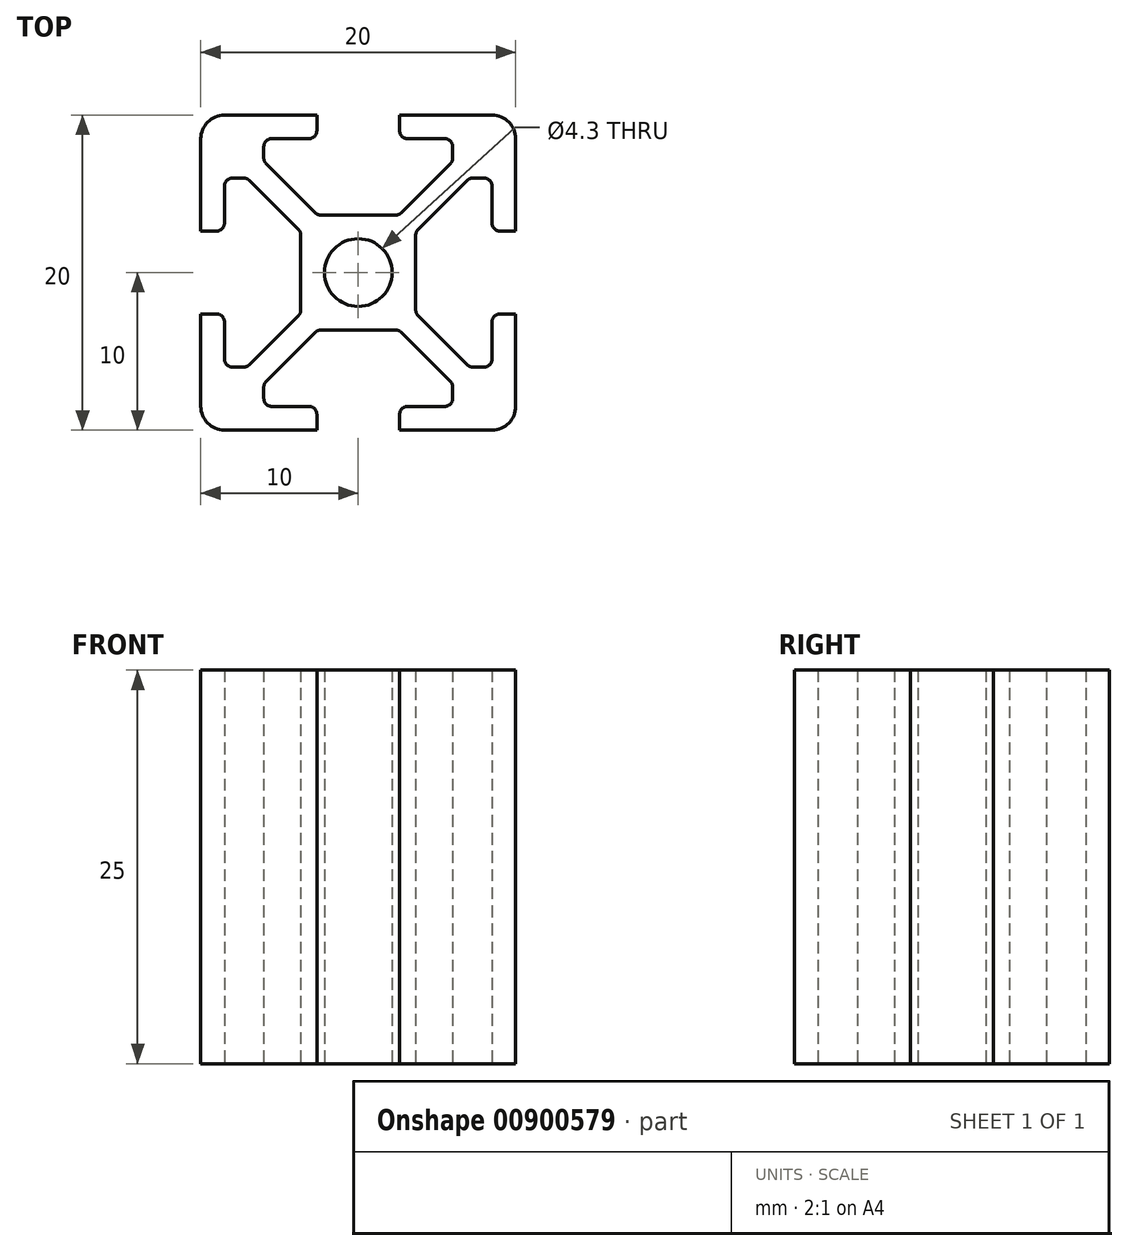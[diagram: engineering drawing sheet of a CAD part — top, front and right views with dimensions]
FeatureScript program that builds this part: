
annotation { "Feature Type Name" : "Feature", "Feature Type Description" : "" }
export const myFeature = defineFeature(function(context is Context, id is Id, definition is map)
    precondition{}
    {
        {
            var Q0;
            Q0=qCreatedBy(makeId("Top.planeOp"),FACE);
            var sketch = newSketch(context, id + "F0", { "sketchPlane" : qUnion([Q0])});
            skPoint(sketch, "E0.middle", {"position": v(0, 0) * mm});
            skCircle(sketch, "E1", {"center": v(0, 0) * mm, "radius": 2.15 * mm});
            skLineSegment(sketch, "E2.bottom", {"start": v(10, 10) * mm, "end": v(-10, 10) * mm});
            skLineSegment(sketch, "E2.top", {"start": v(10, -10) * mm, "end": v(-10, -10) * mm});
            skLineSegment(sketch, "E2.left", {"start": v(10, 10) * mm, "end": v(10, -10) * mm});
            skLineSegment(sketch, "E2.right", {"start": v(-10, 10) * mm, "end": v(-10, -10) * mm});
            skSolve(sketch);
        }
        {
            var Q0;
            Q0=makeQuery(id+"F0.imprint","IMPRINT",FACE,{"disambiguationData":[TD([[makeQuery(id+"F0.imprint","IMPRINT",EDGE,{"derivedFrom":sQuery(id+"F0.wireOp",EDGE,"E1")}),-1.0]])]});
            var sketch = newSketch(context, id + "F1", { "sketchPlane" : qUnion([Q0])});
            skLineSegment(sketch, "E3", {"start": v(-2.63, 10) * mm, "end": v(2.63, 10) * mm});
            skLineSegment(sketch, "E4", {"start": v(2.63, 10) * mm, "end": v(2.63, 8.5) * mm});
            skLineSegment(sketch, "E5", {"start": v(2.63, 8.5) * mm, "end": v(6, 8.5) * mm});
            skLineSegment(sketch, "E6", {"start": v(6, 8.5) * mm, "end": v(6, 7.06) * mm});
            skLineSegment(sketch, "E7", {"start": v(6, 7.06) * mm, "end": v(2.59, 3.65) * mm});
            skLineSegment(sketch, "E8", {"start": v(2.59, 3.65) * mm, "end": v(-2.59, 3.65) * mm});
            skLineSegment(sketch, "E9", {"start": v(-2.59, 3.65) * mm, "end": v(-6, 7.06) * mm});
            skLineSegment(sketch, "E10", {"start": v(-6, 7.06) * mm, "end": v(-6, 8.5) * mm});
            skLineSegment(sketch, "E11", {"start": v(-6, 8.5) * mm, "end": v(-2.63, 8.5) * mm});
            skLineSegment(sketch, "E12", {"start": v(-2.63, 8.5) * mm, "end": v(-2.63, 10) * mm});
            skPoint(sketch, "E13", {"position": v(0, 10) * mm});
            skPoint(sketch, "E14", {"position": v(0, 3.65) * mm});
            skPoint(sketch, "E15.center", {"position": v(0.01, -0.04) * mm});
            skLineSegment(sketch, "E16.0.0", {"start": v(-10, -10) * mm, "end": v(10, -10) * mm});
            skLineSegment(sketch, "E16.0.1", {"start": v(10, -10) * mm, "end": v(10, 10) * mm});
            skLineSegment(sketch, "E16.0.2", {"start": v(10, 10) * mm, "end": v(-10, 10) * mm});
            skLineSegment(sketch, "E16.0.3", {"start": v(-10, 10) * mm, "end": v(-10, -10) * mm});
            skLineSegment(sketch, "E17", {"start": v(0, 0) * mm, "end": v(10, 10) * mm, "construction": true});
            skLineSegment(sketch, "E18.1.0", {"start": v(-8.5, -2.63) * mm, "end": v(-10, -2.63) * mm});
            skLineSegment(sketch, "E18.1.1", {"start": v(-8.5, -6) * mm, "end": v(-8.5, -2.63) * mm});
            skLineSegment(sketch, "E18.1.2", {"start": v(-7.06, -6) * mm, "end": v(-8.5, -6) * mm});
            skLineSegment(sketch, "E18.1.3", {"start": v(-3.65, -2.59) * mm, "end": v(-7.06, -6) * mm});
            skLineSegment(sketch, "E18.1.4", {"start": v(-3.65, 2.59) * mm, "end": v(-3.65, -2.59) * mm});
            skLineSegment(sketch, "E18.1.5", {"start": v(-7.06, 6) * mm, "end": v(-3.65, 2.59) * mm});
            skLineSegment(sketch, "E18.1.6", {"start": v(-8.5, 6) * mm, "end": v(-7.06, 6) * mm});
            skLineSegment(sketch, "E18.1.7", {"start": v(-8.5, 2.63) * mm, "end": v(-8.5, 6) * mm});
            skLineSegment(sketch, "E18.1.8", {"start": v(-10, 2.63) * mm, "end": v(-8.5, 2.63) * mm});
            skLineSegment(sketch, "E18.2.0", {"start": v(2.63, -8.5) * mm, "end": v(2.63, -10) * mm});
            skLineSegment(sketch, "E18.2.1", {"start": v(6, -8.5) * mm, "end": v(2.63, -8.5) * mm});
            skLineSegment(sketch, "E18.2.2", {"start": v(6, -7.06) * mm, "end": v(6, -8.5) * mm});
            skLineSegment(sketch, "E18.2.3", {"start": v(2.59, -3.65) * mm, "end": v(6, -7.06) * mm});
            skLineSegment(sketch, "E18.2.4", {"start": v(-2.59, -3.65) * mm, "end": v(2.59, -3.65) * mm});
            skLineSegment(sketch, "E18.2.5", {"start": v(-6, -7.06) * mm, "end": v(-2.59, -3.65) * mm});
            skLineSegment(sketch, "E18.2.6", {"start": v(-6, -8.5) * mm, "end": v(-6, -7.06) * mm});
            skLineSegment(sketch, "E18.2.7", {"start": v(-2.63, -8.5) * mm, "end": v(-6, -8.5) * mm});
            skLineSegment(sketch, "E18.2.8", {"start": v(-2.63, -10) * mm, "end": v(-2.63, -8.5) * mm});
            skLineSegment(sketch, "E18.3.0", {"start": v(8.5, 2.63) * mm, "end": v(10, 2.63) * mm});
            skLineSegment(sketch, "E18.3.1", {"start": v(8.5, 6) * mm, "end": v(8.5, 2.63) * mm});
            skLineSegment(sketch, "E18.3.2", {"start": v(7.06, 6) * mm, "end": v(8.5, 6) * mm});
            skLineSegment(sketch, "E18.3.3", {"start": v(3.65, 2.59) * mm, "end": v(7.06, 6) * mm});
            skLineSegment(sketch, "E18.3.4", {"start": v(3.65, -2.59) * mm, "end": v(3.65, 2.59) * mm});
            skLineSegment(sketch, "E18.3.5", {"start": v(7.06, -6) * mm, "end": v(3.65, -2.59) * mm});
            skLineSegment(sketch, "E18.3.6", {"start": v(8.5, -6) * mm, "end": v(7.06, -6) * mm});
            skLineSegment(sketch, "E18.3.7", {"start": v(8.5, -2.63) * mm, "end": v(8.5, -6) * mm});
            skLineSegment(sketch, "E18.3.8", {"start": v(10, -2.63) * mm, "end": v(8.5, -2.63) * mm});
            skPoint(sketch, "E18.center", {"position": v(0, 0) * mm});
            skSolve(sketch);
        }
        {
            var Q0;
            Q0=makeQuery(id+"F0.imprint","IMPRINT",FACE,{"disambiguationData":[TD([[makeQuery(id+"F0.imprint","IMPRINT",EDGE,{"derivedFrom":sQuery(id+"F0.wireOp",EDGE,"E1")}),-1.0]])]});
            extrude(context, id + "F2", {"entities" : qUnion([Q0]), "depth" : 25 * mm, "offsetDistance" : 25 * mm});
        }
        {
            var Q0;
            {var subQ0=sQuery(id+"F1.wireOp",EDGE,"E18.1.0");Q0=makeQuery(id+"F1.imprint","IMPRINT",FACE,{"disambiguationData":[TD([[makeQuery(id+"F1.imprint","IMPRINT",EDGE,{"derivedFrom":subQ0}),-1.0]])]});}
            var Q1;
            {var subQ0=sQuery(id+"F1.wireOp",EDGE,"E18.2.0");Q1=makeQuery(id+"F1.imprint","IMPRINT",FACE,{"disambiguationData":[TD([[makeQuery(id+"F1.imprint","IMPRINT",EDGE,{"derivedFrom":subQ0}),-1.0]])]});}
            var Q2;
            {var subQ0=sQuery(id+"F1.wireOp",EDGE,"E18.3.0");Q2=makeQuery(id+"F1.imprint","IMPRINT",FACE,{"disambiguationData":[TD([[makeQuery(id+"F1.imprint","IMPRINT",EDGE,{"derivedFrom":subQ0}),-1.0]])]});}
            var Q3;
            {var subQ0=sQuery(id+"F1.wireOp",EDGE,"E4");Q3=makeQuery(id+"F1.imprint","IMPRINT",FACE,{"disambiguationData":[TD([[makeQuery(id+"F1.imprint","IMPRINT",EDGE,{"derivedFrom":subQ0}),-1.0]])]});}
            extrude(context, id + "F3", {"entities" : qUnion([Q0, Q1, Q2, Q3]), "operationType" : NewBodyOperationType.REMOVE, "endBound" : BoundingType.THROUGH_ALL, "depth" : 25 * mm, "offsetDistance" : 25 * mm});
        }
        {
            var Q0;
            Q0=makeQuery(id+"F2.opExtrude","SWEPT_EDGE",EDGE,{"disambiguationData":[OSD([sQuery(id+"F0.wireOp",EDGE,"E2.top"),sQuery(id+"F0.wireOp",EDGE,"E2.left")])]});
            var Q1;
            Q1=makeQuery(id+"F2.opExtrude","SWEPT_EDGE",EDGE,{"disambiguationData":[OSD([sQuery(id+"F0.wireOp",EDGE,"E2.top"),sQuery(id+"F0.wireOp",EDGE,"E2.right")])]});
            var Q2;
            Q2=makeQuery(id+"F2.opExtrude","SWEPT_EDGE",EDGE,{"disambiguationData":[OSD([sQuery(id+"F0.wireOp",EDGE,"E2.bottom"),sQuery(id+"F0.wireOp",EDGE,"E2.left")])]});
            var Q3;
            Q3=makeQuery(id+"F2.opExtrude","SWEPT_EDGE",EDGE,{"disambiguationData":[OSD([sQuery(id+"F0.wireOp",EDGE,"E2.bottom"),sQuery(id+"F0.wireOp",EDGE,"E2.right")])]});
            fillet(context, id + "F4", {"entities" : qUnion([Q0, Q1, Q2, Q3]), "radius" : 1.5 * mm, "tangentPropagation" : true, "allowEdgeOverflow" : false});
        }
        {
            var Q0;
            Q0=makeQuery(id+"F3.boolean.opBoolean","COPY",EDGE,{"derivedFrom":makeQuery(id+"F3.opExtrude","SWEPT_EDGE",EDGE,{"disambiguationData":[OSD([sQuery(id+"F1.wireOp",EDGE,"E16.0.0"),sQuery(id+"F1.wireOp",EDGE,"E18.2.8")])]})});
            var Q1;
            Q1=makeQuery(id+"F3.boolean.opBoolean","COPY",EDGE,{"derivedFrom":makeQuery(id+"F3.opExtrude","SWEPT_EDGE",EDGE,{"disambiguationData":[OSD([sQuery(id+"F1.wireOp",EDGE,"E16.0.3"),sQuery(id+"F1.wireOp",EDGE,"E18.1.8")])]})});
            var Q2;
            Q2=makeQuery(id+"F3.boolean.opBoolean","COPY",EDGE,{"derivedFrom":makeQuery(id+"F3.opExtrude","SWEPT_EDGE",EDGE,{"disambiguationData":[OSD([sQuery(id+"F1.wireOp",EDGE,"E12"),sQuery(id+"F1.wireOp",EDGE,"E16.0.2")])]})});
            var Q3;
            Q3=makeQuery(id+"F3.boolean.opBoolean","COPY",EDGE,{"derivedFrom":makeQuery(id+"F3.opExtrude","SWEPT_EDGE",EDGE,{"disambiguationData":[OSD([sQuery(id+"F1.wireOp",EDGE,"E16.0.0"),sQuery(id+"F1.wireOp",EDGE,"E18.2.0")])]})});
            var Q4;
            Q4=makeQuery(id+"F3.boolean.opBoolean","COPY",EDGE,{"derivedFrom":makeQuery(id+"F3.opExtrude","SWEPT_EDGE",EDGE,{"disambiguationData":[OSD([sQuery(id+"F1.wireOp",EDGE,"E16.0.1"),sQuery(id+"F1.wireOp",EDGE,"E18.3.0")])]})});
            var Q5;
            Q5=makeQuery(id+"F3.boolean.opBoolean","COPY",EDGE,{"derivedFrom":makeQuery(id+"F3.opExtrude","SWEPT_EDGE",EDGE,{"disambiguationData":[OSD([sQuery(id+"F1.wireOp",EDGE,"E16.0.1"),sQuery(id+"F1.wireOp",EDGE,"E18.3.8")])]})});
            var Q6;
            Q6=makeQuery(id+"F3.boolean.opBoolean","COPY",EDGE,{"derivedFrom":makeQuery(id+"F3.opExtrude","SWEPT_EDGE",EDGE,{"disambiguationData":[OSD([sQuery(id+"F1.wireOp",EDGE,"E16.0.3"),sQuery(id+"F1.wireOp",EDGE,"E18.1.0")])]})});
            var Q7;
            Q7=makeQuery(id+"F3.boolean.opBoolean","COPY",EDGE,{"derivedFrom":makeQuery(id+"F3.opExtrude","SWEPT_EDGE",EDGE,{"disambiguationData":[OSD([sQuery(id+"F1.wireOp",EDGE,"E4"),sQuery(id+"F1.wireOp",EDGE,"E16.0.2")])]})});
            var Q8;
            Q8=makeQuery(id+"F3.boolean.opBoolean","COPY",EDGE,{"derivedFrom":makeQuery(id+"F3.opExtrude","SWEPT_EDGE",EDGE,{"disambiguationData":[OSD([sQuery(id+"F1.wireOp",EDGE,"E18.2.6"),sQuery(id+"F1.wireOp",EDGE,"E18.2.7")])]})});
            var Q9;
            Q9=makeQuery(id+"F3.boolean.opBoolean","COPY",EDGE,{"derivedFrom":makeQuery(id+"F3.opExtrude","SWEPT_EDGE",EDGE,{"disambiguationData":[OSD([sQuery(id+"F1.wireOp",EDGE,"E18.2.7"),sQuery(id+"F1.wireOp",EDGE,"E18.2.8")])]})});
            var Q10;
            Q10=makeQuery(id+"F3.boolean.opBoolean","COPY",EDGE,{"derivedFrom":makeQuery(id+"F3.opExtrude","SWEPT_EDGE",EDGE,{"disambiguationData":[OSD([sQuery(id+"F1.wireOp",EDGE,"E18.2.0"),sQuery(id+"F1.wireOp",EDGE,"E18.2.1")])]})});
            var Q11;
            Q11=makeQuery(id+"F3.boolean.opBoolean","COPY",EDGE,{"derivedFrom":makeQuery(id+"F3.opExtrude","SWEPT_EDGE",EDGE,{"disambiguationData":[OSD([sQuery(id+"F1.wireOp",EDGE,"E18.1.7"),sQuery(id+"F1.wireOp",EDGE,"E18.1.8")])]})});
            var Q12;
            Q12=makeQuery(id+"F3.boolean.opBoolean","COPY",EDGE,{"derivedFrom":makeQuery(id+"F3.opExtrude","SWEPT_EDGE",EDGE,{"disambiguationData":[OSD([sQuery(id+"F1.wireOp",EDGE,"E18.1.0"),sQuery(id+"F1.wireOp",EDGE,"E18.1.1")])]})});
            var Q13;
            Q13=makeQuery(id+"F3.boolean.opBoolean","COPY",EDGE,{"derivedFrom":makeQuery(id+"F3.opExtrude","SWEPT_EDGE",EDGE,{"disambiguationData":[OSD([sQuery(id+"F1.wireOp",EDGE,"E18.3.7"),sQuery(id+"F1.wireOp",EDGE,"E18.3.8")])]})});
            var Q14;
            Q14=makeQuery(id+"F3.boolean.opBoolean","COPY",EDGE,{"derivedFrom":makeQuery(id+"F3.opExtrude","SWEPT_EDGE",EDGE,{"disambiguationData":[OSD([sQuery(id+"F1.wireOp",EDGE,"E18.3.0"),sQuery(id+"F1.wireOp",EDGE,"E18.3.1")])]})});
            var Q15;
            Q15=makeQuery(id+"F3.boolean.opBoolean","COPY",EDGE,{"derivedFrom":makeQuery(id+"F3.opExtrude","SWEPT_EDGE",EDGE,{"disambiguationData":[OSD([sQuery(id+"F1.wireOp",EDGE,"E4"),sQuery(id+"F1.wireOp",EDGE,"E5")])]})});
            var Q16;
            Q16=makeQuery(id+"F3.boolean.opBoolean","COPY",EDGE,{"derivedFrom":makeQuery(id+"F3.opExtrude","SWEPT_EDGE",EDGE,{"disambiguationData":[OSD([sQuery(id+"F1.wireOp",EDGE,"E5"),sQuery(id+"F1.wireOp",EDGE,"E6")])]})});
            var Q17;
            Q17=makeQuery(id+"F3.boolean.opBoolean","COPY",EDGE,{"derivedFrom":makeQuery(id+"F3.opExtrude","SWEPT_EDGE",EDGE,{"disambiguationData":[OSD([sQuery(id+"F1.wireOp",EDGE,"E18.3.1"),sQuery(id+"F1.wireOp",EDGE,"E18.3.2")])]})});
            var Q18;
            Q18=makeQuery(id+"F3.boolean.opBoolean","COPY",EDGE,{"derivedFrom":makeQuery(id+"F3.opExtrude","SWEPT_EDGE",EDGE,{"disambiguationData":[OSD([sQuery(id+"F1.wireOp",EDGE,"E18.3.2"),sQuery(id+"F1.wireOp",EDGE,"E18.3.3")])]})});
            var Q19;
            Q19=makeQuery(id+"F3.boolean.opBoolean","COPY",EDGE,{"derivedFrom":makeQuery(id+"F3.opExtrude","SWEPT_EDGE",EDGE,{"disambiguationData":[OSD([sQuery(id+"F1.wireOp",EDGE,"E6"),sQuery(id+"F1.wireOp",EDGE,"E7")])]})});
            var Q20;
            Q20=makeQuery(id+"F3.boolean.opBoolean","COPY",EDGE,{"derivedFrom":makeQuery(id+"F3.opExtrude","SWEPT_EDGE",EDGE,{"disambiguationData":[OSD([sQuery(id+"F1.wireOp",EDGE,"E18.2.4"),sQuery(id+"F1.wireOp",EDGE,"E18.2.5")])]})});
            var Q21;
            Q21=makeQuery(id+"F3.boolean.opBoolean","COPY",EDGE,{"derivedFrom":makeQuery(id+"F3.opExtrude","SWEPT_EDGE",EDGE,{"disambiguationData":[OSD([sQuery(id+"F1.wireOp",EDGE,"E18.2.3"),sQuery(id+"F1.wireOp",EDGE,"E18.2.4")])]})});
            var Q22;
            Q22=makeQuery(id+"F3.boolean.opBoolean","COPY",EDGE,{"derivedFrom":makeQuery(id+"F3.opExtrude","SWEPT_EDGE",EDGE,{"disambiguationData":[OSD([sQuery(id+"F1.wireOp",EDGE,"E18.3.3"),sQuery(id+"F1.wireOp",EDGE,"E18.3.4")])]})});
            var Q23;
            Q23=makeQuery(id+"F3.boolean.opBoolean","COPY",EDGE,{"derivedFrom":makeQuery(id+"F3.opExtrude","SWEPT_EDGE",EDGE,{"disambiguationData":[OSD([sQuery(id+"F1.wireOp",EDGE,"E18.3.4"),sQuery(id+"F1.wireOp",EDGE,"E18.3.5")])]})});
            var Q24;
            Q24=makeQuery(id+"F3.boolean.opBoolean","COPY",EDGE,{"derivedFrom":makeQuery(id+"F3.opExtrude","SWEPT_EDGE",EDGE,{"disambiguationData":[OSD([sQuery(id+"F1.wireOp",EDGE,"E18.1.3"),sQuery(id+"F1.wireOp",EDGE,"E18.1.4")])]})});
            var Q25;
            Q25=makeQuery(id+"F3.boolean.opBoolean","COPY",EDGE,{"derivedFrom":makeQuery(id+"F3.opExtrude","SWEPT_EDGE",EDGE,{"disambiguationData":[OSD([sQuery(id+"F1.wireOp",EDGE,"E18.1.4"),sQuery(id+"F1.wireOp",EDGE,"E18.1.5")])]})});
            var Q26;
            Q26=makeQuery(id+"F3.boolean.opBoolean","COPY",EDGE,{"derivedFrom":makeQuery(id+"F3.opExtrude","SWEPT_EDGE",EDGE,{"disambiguationData":[OSD([sQuery(id+"F1.wireOp",EDGE,"E7"),sQuery(id+"F1.wireOp",EDGE,"E8")])]})});
            var Q27;
            Q27=makeQuery(id+"F3.boolean.opBoolean","COPY",EDGE,{"derivedFrom":makeQuery(id+"F3.opExtrude","SWEPT_EDGE",EDGE,{"disambiguationData":[OSD([sQuery(id+"F1.wireOp",EDGE,"E8"),sQuery(id+"F1.wireOp",EDGE,"E9")])]})});
            var Q28;
            Q28=makeQuery(id+"F3.boolean.opBoolean","COPY",EDGE,{"derivedFrom":makeQuery(id+"F3.opExtrude","SWEPT_EDGE",EDGE,{"disambiguationData":[OSD([sQuery(id+"F1.wireOp",EDGE,"E10"),sQuery(id+"F1.wireOp",EDGE,"E11")])]})});
            var Q29;
            Q29=makeQuery(id+"F3.boolean.opBoolean","COPY",EDGE,{"derivedFrom":makeQuery(id+"F3.opExtrude","SWEPT_EDGE",EDGE,{"disambiguationData":[OSD([sQuery(id+"F1.wireOp",EDGE,"E9"),sQuery(id+"F1.wireOp",EDGE,"E10")])]})});
            var Q30;
            Q30=makeQuery(id+"F3.boolean.opBoolean","COPY",EDGE,{"derivedFrom":makeQuery(id+"F3.opExtrude","SWEPT_EDGE",EDGE,{"disambiguationData":[OSD([sQuery(id+"F1.wireOp",EDGE,"E11"),sQuery(id+"F1.wireOp",EDGE,"E12")])]})});
            var Q31;
            Q31=makeQuery(id+"F3.boolean.opBoolean","COPY",EDGE,{"derivedFrom":makeQuery(id+"F3.opExtrude","SWEPT_EDGE",EDGE,{"disambiguationData":[OSD([sQuery(id+"F1.wireOp",EDGE,"E18.3.6"),sQuery(id+"F1.wireOp",EDGE,"E18.3.7")])]})});
            var Q32;
            Q32=makeQuery(id+"F3.boolean.opBoolean","COPY",EDGE,{"derivedFrom":makeQuery(id+"F3.opExtrude","SWEPT_EDGE",EDGE,{"disambiguationData":[OSD([sQuery(id+"F1.wireOp",EDGE,"E18.3.5"),sQuery(id+"F1.wireOp",EDGE,"E18.3.6")])]})});
            var Q33;
            Q33=makeQuery(id+"F3.boolean.opBoolean","COPY",EDGE,{"derivedFrom":makeQuery(id+"F3.opExtrude","SWEPT_EDGE",EDGE,{"disambiguationData":[OSD([sQuery(id+"F1.wireOp",EDGE,"E18.1.1"),sQuery(id+"F1.wireOp",EDGE,"E18.1.2")])]})});
            var Q34;
            Q34=makeQuery(id+"F3.boolean.opBoolean","COPY",EDGE,{"derivedFrom":makeQuery(id+"F3.opExtrude","SWEPT_EDGE",EDGE,{"disambiguationData":[OSD([sQuery(id+"F1.wireOp",EDGE,"E18.1.2"),sQuery(id+"F1.wireOp",EDGE,"E18.1.3")])]})});
            var Q35;
            Q35=makeQuery(id+"F3.boolean.opBoolean","COPY",EDGE,{"derivedFrom":makeQuery(id+"F3.opExtrude","SWEPT_EDGE",EDGE,{"disambiguationData":[OSD([sQuery(id+"F1.wireOp",EDGE,"E18.2.5"),sQuery(id+"F1.wireOp",EDGE,"E18.2.6")])]})});
            var Q36;
            Q36=makeQuery(id+"F3.boolean.opBoolean","COPY",EDGE,{"derivedFrom":makeQuery(id+"F3.opExtrude","SWEPT_EDGE",EDGE,{"disambiguationData":[OSD([sQuery(id+"F1.wireOp",EDGE,"E18.2.2"),sQuery(id+"F1.wireOp",EDGE,"E18.2.3")])]})});
            var Q37;
            Q37=makeQuery(id+"F3.boolean.opBoolean","COPY",EDGE,{"derivedFrom":makeQuery(id+"F3.opExtrude","SWEPT_EDGE",EDGE,{"disambiguationData":[OSD([sQuery(id+"F1.wireOp",EDGE,"E18.2.1"),sQuery(id+"F1.wireOp",EDGE,"E18.2.2")])]})});
            var Q38;
            Q38=makeQuery(id+"F3.boolean.opBoolean","COPY",EDGE,{"derivedFrom":makeQuery(id+"F3.opExtrude","SWEPT_EDGE",EDGE,{"disambiguationData":[OSD([sQuery(id+"F1.wireOp",EDGE,"E18.1.6"),sQuery(id+"F1.wireOp",EDGE,"E18.1.7")])]})});
            var Q39;
            Q39=makeQuery(id+"F3.boolean.opBoolean","COPY",EDGE,{"derivedFrom":makeQuery(id+"F3.opExtrude","SWEPT_EDGE",EDGE,{"disambiguationData":[OSD([sQuery(id+"F1.wireOp",EDGE,"E18.1.5"),sQuery(id+"F1.wireOp",EDGE,"E18.1.6")])]})});
            fillet(context, id + "F5", {"entities" : qUnion([Q0, Q1, Q2, Q3, Q4, Q5, Q6, Q7, Q8, Q9, Q10, Q11, Q12, Q13, Q14, Q15, Q16, Q17, Q18, Q19, Q20, Q21, Q22, Q23, Q24, Q25, Q26, Q27, Q28, Q29, Q30, Q31, Q32, Q33, Q34, Q35, Q36, Q37, Q38, Q39]), "radius" : 0.5 * mm, "tangentPropagation" : true, "allowEdgeOverflow" : false});
        }
    });
